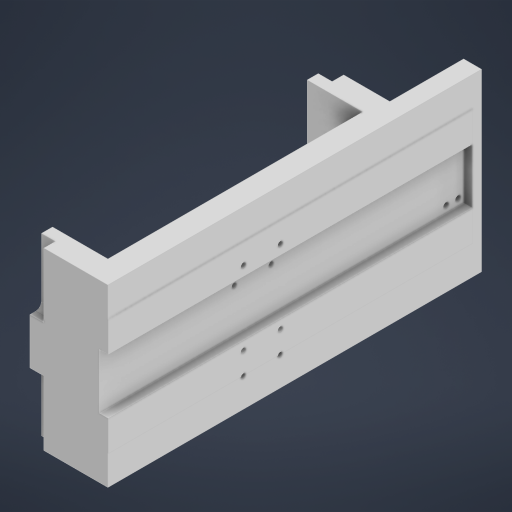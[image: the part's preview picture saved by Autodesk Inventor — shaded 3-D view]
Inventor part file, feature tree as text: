
AUTODESK INVENTOR PART (.ipt)
format: ipt  version: 2024 (Build 280153000, 153)  size: 359,424 bytes
history: native  units: mm
features: extrude x10, sketch x10, projected_geometry x5, other x1, fillet x1
ambient origin geometry x8: Origin, YZ Plane, XZ Plane, XY Plane, X Axis, Y Axis, Z Axis, Center Point
bodies: Body1 (feature_tree)
feature tree (27):
  other  "Твердое тело1"
  extrude  "Выдавливание1"  Depth=60.0mm
  extrude  "Выдавливание2"  Depth=25.0mm
  extrude  "Выдавливание3"  Depth=25.0mm
  extrude  "Выдавливание4"  Depth=190.0mm TaperAngle=0.0deg
  extrude  "Выдавливание5"  Depth=32.0mm
  fillet  "Сопряжение1"  Radius=32.0mm
  extrude  "Выдавливание6"  Depth=0.5mm TaperAngle=0.0deg
  extrude  "Выдавливание7"  Depth=20.0mm
  extrude  "Выдавливание8"  Depth=70.0mm TaperAngle=0.0deg
  extrude  "Extrusion9"  Depth=33.0mm
  extrude  "Extrusion10"  Depth=33.0mm
  sketch  "Эскиз1"
  sketch  "Эскиз2"
  projected_geometry  "Спроецированная петля1"
  sketch  "Эскиз4"
  projected_geometry  "Спроецированная петля3"
  sketch  "Эскиз5"
  projected_geometry  "Спроецированная петля4"
  sketch  "Эскиз6"
  projected_geometry  "Спроецированная петля5"
  projected_geometry  "Спроецированная петля6"
  sketch  "Эскиз8"
  sketch  "Эскиз9"
  sketch  "Эскиз10"
  sketch  "Sketch11"  dims[d0=300.0mm d1=60.0mm]
  sketch  "Sketch12"  dims[d2=25.0mm d3=25.0mm d5=25.0mm d6=190.0mm d7=0.0mm d8=32.0mm d9=32.0mm d10=0.5mm d11=0.0mm d12=20.0mm d13=70.0mm d14=0.0mm d15=33.0mm d16=33.0mm d17=10.0mm d18=0.0mm d19=15.0mm d20=0.0mm d21=70.0mm d22=70.0mm d23=6.0mm d24=6.0mm d25=46.0mm d26=13.0mm d27=100.0mm d28=0.0mm d29=10.0mm d30=0.0mm d31=33.0mm d32=0.0mm d33=25.0mm d34=24.5mm d35=24.5mm d36=0.5mm d37=0.5mm d38=200.0mm d39=0.0mm d40=80.0mm d41=80.0mm d42=80.0mm d43=80.0mm d44=40.0mm d45=0.0mm d46=12.0mm d47=12.0mm]
